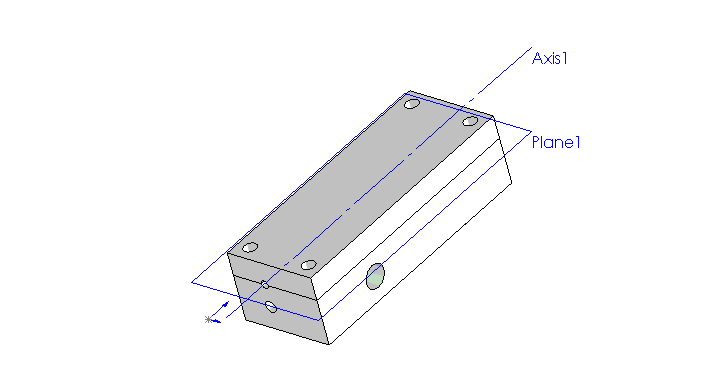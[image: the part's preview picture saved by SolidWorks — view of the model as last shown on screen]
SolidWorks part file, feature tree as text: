
SOLIDWORKS PART (.sldprt)
format: sldprt  version: not decoded by parser v0  size: 120,320 bytes
history: native  units: mm
features: sketch x6, cut_extrude x5, extrude x1, plane x1 (+11 scaffold rows collapsed)
feature tree (24):
  scaffold x11  (default folders/planes/origin — collapsed)
  sketch  "Sketch1"  dims[D1=66.675mm D2=25.4mm]
  extrude  "Extrude1"  Depth=19.05mm
  sketch  "Sketch2"  dims[D1=6.35mm D2=9.525mm D3=6.35mm]
  cut_extrude  "Cut-Extrude1"  Depth=63.5mm
  sketch  "Sketch3"  dims[D1=3.175mm D2=6.35mm]
  cut_extrude  "Cut-Extrude2"  [1 undecoded]
  sketch  "Sketch4"  dims[D1=6.35mm D2=19.05mm]
  cut_extrude  "Cut-Extrude3"  Depth=10.16mm
  sketch  "Sketch5"  dims[c1.D1=3.4925mm c1.D4=3.4925mm c1.D6=3.4925mm c1.D2=3.81mm c1.D3=3.81mm c1.D5=3.81mm c2.D6=33.3375mm]
  cut_extrude  "Cut-Extrude4"  [1 undecoded]
  sketch  "Sketch6"  dims[D1=2.1082mm D2=6.35mm]
  cut_extrude  "Cut-Extrude6"  [1 undecoded]
  plane  "Plane1"  Offset=12.7mm
decode coverage: 9 of 12 modeling features carry decoded parameters
note: 3 parameter values undecoded
summary: no parameter record found for 3 features
note: suppression state not decoded; provenance and decode notes live in map.json
